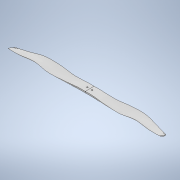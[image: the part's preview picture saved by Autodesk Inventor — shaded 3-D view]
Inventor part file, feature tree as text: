
AUTODESK INVENTOR PART (.ipt)
format: ipt  version: 2020 (Build 240168000, 168)  size: 260,608 bytes
history: native  units: in
note: dims shown in document units (in); Inventor stores cm internally (conversion verified against a paired STEP export)
features: sketch x8, plane x6, loft x1, extrude x1, mirror x1
ambient origin geometry x8: Origin, YZ Plane, XZ Plane, XY Plane, X Axis, Y Axis, Z Axis, Center Point
bodies: Solid1 (feature_tree)
feature tree (17):
  sketch  "Sketch1"  dims[d0=0.1335in d1=0.875in]
  plane  "Work Plane6"
  loft  "Loft1"
  extrude  "Extrusion1"  Depth=1.5in
  mirror  "Mirror1"
  plane  "Work Plane1"
  plane  "Work Plane2"
  plane  "Work Plane3"
  plane  "Work Plane4"
  plane  "Work Plane5"
  sketch  "Sketch2"  dims[d2=0.5in d3=1.5in]
  sketch  "Sketch3"  dims[d4=1.5in]
  sketch  "Sketch4"  dims[d5=1.5in]
  sketch  "Sketch5"  dims[d6=1.5in d7=1.0in]
  sketch  "Sketch6"  dims[d8=0.0in d9=90.0deg]
  sketch  "Sketch7"  dims[d10=0.0in d11=90.0deg]
  sketch  "Sketch8"  dims[d12=0.0in d13=90.0deg d14=0.0in d15=90.0deg d16=0.0in d17=90.0deg d18=0.0in d19=90.0deg d20=0.0in d21=90.0deg d22=0.2333in d23=0.125in d24=0.07in d25=0.0in]
